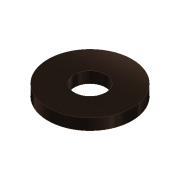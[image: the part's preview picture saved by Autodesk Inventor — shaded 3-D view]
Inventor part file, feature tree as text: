
AUTODESK INVENTOR PART (.ipt)
format: ipt  version: 2017 (Build 210142000, 142)  size: 82,432 bytes
history: native  units: mm
features: extrude x1, sketch x1
ambient origin geometry x8: Origin, YZ Plane, XZ Plane, XY Plane, X Axis, Y Axis, Z Axis, Center Point
bodies: Solid1 (feature_tree)
feature tree (2):
  extrude  "Extrusion1"  Depth=1.0mm
  sketch  "Sketch1"  dims[d0=7.5mm d1=2.8mm d2=1.0mm d3=0.0mm]
